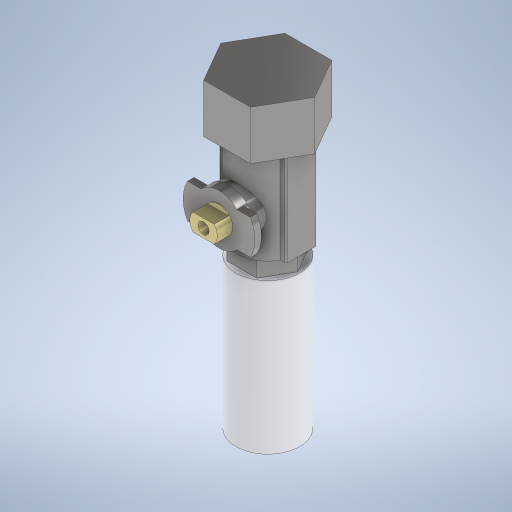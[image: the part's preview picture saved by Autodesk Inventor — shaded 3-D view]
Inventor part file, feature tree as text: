
AUTODESK INVENTOR PART (.ipt)
format: ipt  version: 2023.1 (Build 271208000, 208)  size: 376,832 bytes
history: native  units: mm
features: sketch x9, extrude x8, other x1, fillet x1, revolve x1, projected_geometry x1
ambient origin geometry x8: Origin, YZ Plane, XZ Plane, XY Plane, X Axis, Y Axis, Z Axis, Center Point
bodies: Body1 (feature_tree)
feature tree (21):
  other  "솔리드1"
  extrude  "돌출1"  Depth=25.0mm
  extrude  "돌출2"  Depth=13.0mm TaperAngle=0.0deg
  extrude  "돌출3"  Depth=17.0mm
  extrude  "돌출4"  Depth=18.0mm
  fillet  "모깎기1"  Radius=8.3mm
  sketch  "스케치5"
  revolve  "회전1"
  extrude  "돌출7"  Depth=25.0mm TaperAngle=0.0deg
  sketch  "스케치9"
  extrude  "돌출8"  Depth=16.0mm
  extrude  "돌출9"  Depth=4.5mm TaperAngle=0.0deg
  extrude  "돌출10"  Depth=17.0mm
  sketch  "스케치11"
  sketch  "스케치1"
  sketch  "스케치2"
  sketch  "스케치3"
  sketch  "스케치4"
  sketch  "스케치8"
  projected_geometry  "투영된 루프1"
  sketch  "스케치10"
